# Revit family: Faucet-Deck_Mount-Bath-KOHLER-Loure-K-14675
name_source: partatom
category: Plumbing Fixtures
revit_build: Autodesk Revit 2015 (Build: 20140606_1530(x64)
units: mm (PartAtom-declared; Revit-internal decimal feet)

## types (3) — shared parameters
ADA Compliant = No
Assembly Code = D2010
CW Connection = Yes
Cold Water Inlet = Cold Water Inlet
Date Modified = 02/13/2019
Default Elevation = 36"
Description = Deck-mount high-flow bath faucet
Drain Included = No
Flow Rate = 15 GPM
HW Connection = Yes
Handle Clearance = 3 3/16"
Height = 14 7/16"
Hot Water Inlet = Hot Water Inlet
Length = 6 1/2"
Manufacturer = KOHLER Co.
MasterFormat 1995 = 15410
MasterFormat 2004 = 22.41.39
Material = Premium Metal Construction
Pressure = 45.00 psi
Product Documentation Link = https://www.us.kohler.com
Product Name = Loure
Product Page URL = http://www.us.kohler.com
Spout Reach = 6 1/2"
URL = https://www.us.kohler.com
Vent Connection = No
Waste Connection = No
Waste Water Outlet = Waste Water Outlet
WaterSense Certified = No
Width = 3 3/16"

## per-type parameters (varying)
| type | Finish | Model | Type |
| CP- Polished Chrome | Kohler-Metal-CP-Polished_Chrome | K-14675-4-CP | 1 |
| SN- Vibrant Polished Nickel | Kohler-Metal-SN-Vibrant_Polished_Nickel | K-14675-4-SN | 2 |
| BN- Vibrant Brushed Nickel | Kohler-Metal-BN-Vibrant_Brushed_Nickel | K-14675-4-BN | 3 |

## geometry (parser evidence)
native form markers: Sweep x9
no freeform markers — native parametric forms only
